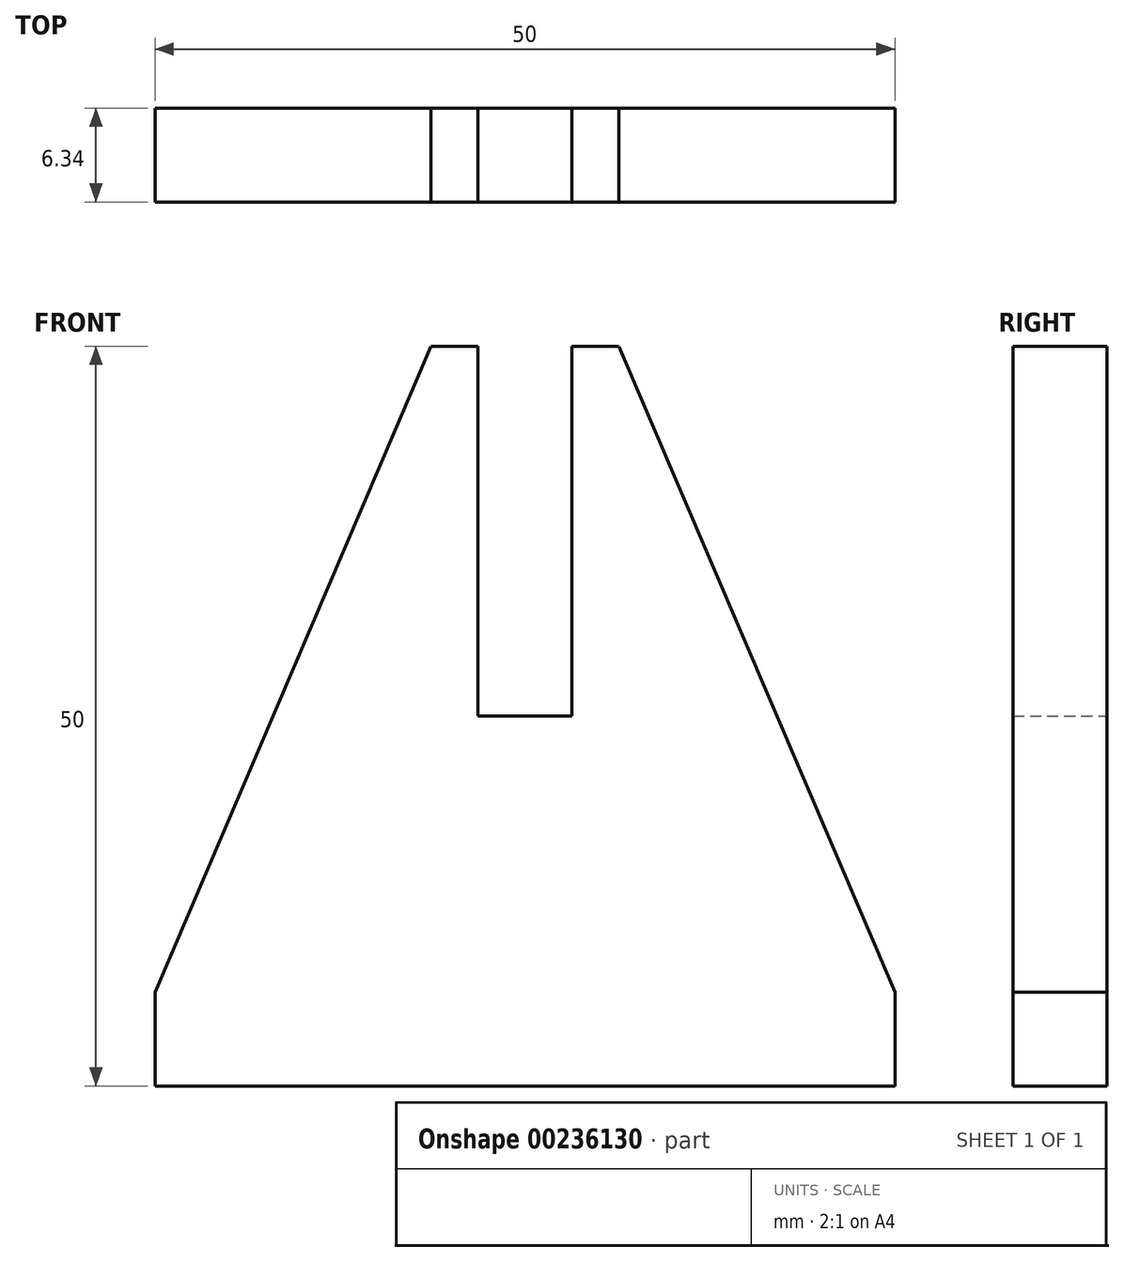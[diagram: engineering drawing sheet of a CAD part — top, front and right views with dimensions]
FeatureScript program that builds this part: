
annotation { "Feature Type Name" : "Feature", "Feature Type Description" : "" }
export const myFeature = defineFeature(function(context is Context, id is Id, definition is map)
    precondition{}
    {
        {
            var Q0;
            Q0=qCreatedBy(makeId("Front.planeOp"),FACE);
            var sketch = newSketch(context, id + "F0", { "sketchPlane" : qUnion([Q0])});
            skLineSegment(sketch, "E0.bottom", {"start": v(-25, 25) * mm, "end": v(25, 25) * mm, "construction": true});
            skLineSegment(sketch, "E0.top", {"start": v(-25, -25) * mm, "end": v(25, -25) * mm, "construction": true});
            skLineSegment(sketch, "E0.left", {"start": v(-25, 25) * mm, "end": v(-25, -25) * mm, "construction": true});
            skLineSegment(sketch, "E0.right", {"start": v(25, 25) * mm, "end": v(25, -25) * mm, "construction": true});
            skPoint(sketch, "E0.middle", {"position": v(0, 0) * mm});
            skLineSegment(sketch, "E1", {"start": v(-25, -25) * mm, "end": v(-25, -18.65) * mm});
            skLineSegment(sketch, "E2", {"start": v(-25, -18.65) * mm, "end": v(-6.35, 25) * mm});
            skLineSegment(sketch, "E3", {"start": v(0, 25) * mm, "end": v(0, -25) * mm, "construction": true});
            skLineSegment(sketch, "E4", {"start": v(-6.35, 25) * mm, "end": v(-3.18, 25) * mm});
            skLineSegment(sketch, "E5", {"start": v(-3.18, 25) * mm, "end": v(-3.17, 0) * mm});
            skLineSegment(sketch, "E6", {"start": v(-3.17, 0) * mm, "end": v(0, 0) * mm});
            skLineSegment(sketch, "E7", {"start": v(-25, -25) * mm, "end": v(0, -25) * mm});
            skLineSegment(sketch, "E8.MirrorCS", {"start": v(3.17, 0) * mm, "end": v(0, 0) * mm});
            skLineSegment(sketch, "E9.MirrorCS", {"start": v(3.17, 25) * mm, "end": v(3.18, 0) * mm});
            skLineSegment(sketch, "E10.MirrorCS", {"start": v(6.35, 25) * mm, "end": v(3.18, 25) * mm});
            skLineSegment(sketch, "E11.MirrorCS", {"start": v(25, -18.65) * mm, "end": v(6.35, 25) * mm});
            skLineSegment(sketch, "E12.MirrorCS", {"start": v(25, -25) * mm, "end": v(25, -18.65) * mm});
            skLineSegment(sketch, "E13.MirrorCS", {"start": v(25, -25) * mm, "end": v(0, -25) * mm});
            skSolve(sketch);
        }
        {
            var Q0;
            Q0 = qSketchRegion(id + "F0", true);
            extrude(context, id + "F1", {"entities" : qUnion([Q0]), "depth" : 6.35 * mm, "symmetric" : true});
        }
    });
